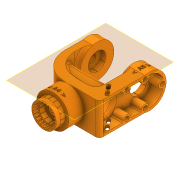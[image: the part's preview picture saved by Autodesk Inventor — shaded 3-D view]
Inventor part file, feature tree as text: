
AUTODESK INVENTOR PART (.ipt)
format: ipt  version: 2020 (Build 240168000, 168)  size: 2,027,008 bytes
history: native  units: in
note: dims shown in document units (in); Inventor stores cm internally (conversion verified against a paired STEP export)
features: sketch x40, extrude x36, projected_geometry x29, chamfer x6, plane x6, fillet x5, emboss x3
ambient origin geometry x8: Origin, YZ Plane, XZ Plane, XY Plane, X Axis, Y Axis, Z Axis, Center Point
bodies: Solid1 (feature_tree)
feature tree (125):
  extrude  "Extrusion1"  Depth=2.0472in
  extrude  "Extrusion2"  Depth=1.1024in
  chamfer  "Chamfer2"  Distance=0.2756in
  extrude  "Extrusion4"  Depth=0.0157in
  extrude  "Extrusion7"  Depth=0.2756in TaperAngle=0.0deg
  chamfer  "Chamfer4"  Distance=0.0394in
  extrude  "Extrusion8"  Depth=0.0157in
  sketch  "Sketch12"  dims[d39=1.4567in d57=0.0394in d58=0.0in]
  plane  "Work Plane1"
  sketch  "Sketch13"  dims[d59=0.315in d60=0.125in d61=0.0137in d67=0.0157in]
  extrude  "Extrusion10"  Depth=0.0394in TaperAngle=0.0deg
  extrude  "Extrusion11"  Depth=0.0866in
  chamfer  "Chamfer5"  Distance=9.4488in Angle=360.0deg
  extrude  "Extrusion12"  Depth=0.2756in TaperAngle=0.0deg
  plane  "Work Plane2"
  extrude  "Extrusion13"  Depth=0.2756in
  plane  "Work Plane3"
  extrude  "Extrusion14"  Depth=1.0236in
  extrude  "Extrusion15"  Depth=0.8858in
  extrude  "Extrusion16"  Depth=0.3937in
  extrude  "Extrusion17"  Depth=1.378in
  sketch  "Sketch21"  dims[d107=0.2756in d108=0.0in d109=0.2756in d110=0.125in d111=0.0137in]
  extrude  "Extrusion19"  Depth=0.5906in
  sketch  "Sketch23"  dims[d112=1.0in d113=0.0in d114=1.0236in]
  extrude  "Extrusion20"  Depth=0.1575in TaperAngle=0.0deg
  extrude  "Extrusion21"  Depth=0.1575in TaperAngle=0.0deg
  extrude  "Extrusion22"  Depth=4.2323in
  extrude  "Extrusion23"  Depth=0.1575in
  extrude  "Extrusion24"  Depth=1.1024in
  extrude  "Extrusion25"  Depth=0.4921in
  extrude  "Extrusion26"  Depth=0.75in
  extrude  "Extrusion27"  Depth=0.2165in TaperAngle=0.0deg
  extrude  "Extrusion28"  Depth=0.1575in
  extrude  "Extrusion29"  Depth=1.1811in
  plane  "Work Plane4"
  extrude  "Extrusion30"  Depth=0.3937in TaperAngle=0.0deg
  fillet  "Fillet1"  Radius=0.3937in
  fillet  "Fillet2"  Radius=0.315in
  extrude  "Extrusion31"  Depth=0.315in TaperAngle=0.0deg
  extrude  "Extrusion32"  Depth=0.315in TaperAngle=0.0deg
  extrude  "Extrusion33"  Depth=0.3937in TaperAngle=0.0deg
  fillet  "Fillet3"  Radius=0.2165in
  extrude  "Extrusion34"  Depth=0.4724in
  chamfer  "Chamfer6"  Distance=0.2756in
  chamfer  "Chamfer7"  Distance=0.0394in
  extrude  "Extrusion35"  Depth=0.001in
  extrude  "Extrusion36"  Depth=1.0in TaperAngle=0.0deg
  fillet  "Fillet5"  Radius=0.1575in
  extrude  "Extrusion38"  Depth=0.315in
  extrude  "Extrusion39"  Depth=0.315in
  extrude  "Extrusion40"  Depth=0.0157in
  fillet  "Fillet7"  Radius=2.3622in
  extrude  "Extrusion41"  Depth=1.0in TaperAngle=0.0deg
  chamfer  "Chamfer8"  Distance=1.0in
  extrude  "Extrusion42"  Depth=0.1969in
  plane  "Work Plane6"
  emboss  "Emboss1"
  emboss  "Emboss2"
  plane  "Work Plane7"
  emboss  "Emboss3"
  sketch  "Sketch1"  dims[d0=0.6299in d1=2.0472in]
  sketch  "Sketch2"  dims[d2=0.9449in d3=0.0in d4=1.1024in]
  sketch  "Sketch4"  dims[d5=1.5748in d6=0.2756in d7=0.0in]
  sketch  "Sketch8"  dims[d11=0.2756in d12=0.125in d13=0.0137in d25=0.0157in]
  projected_geometry  "Projected Loop2"
  sketch  "Sketch10"  dims[d26=6.2992in d28=360.0deg d30=0.2756in d31=0.0in]
  sketch  "Sketch14"  dims[d68=4.7244in d70=360.0deg d72=0.0394in d73=0.0in]
  sketch  "Sketch15"  dims[d83=0.0591in d84=0.0866in]
  projected_geometry  "Projected Loop4"
  sketch  "Sketch16"  dims[d85=0.0827in]
  sketch  "Sketch17"  dims[d86=0.0827in]
  projected_geometry  "Projected Loop5"
  sketch  "Sketch18"  dims[d87=0.0827in d88=9.4488in d90=360.0deg]
  projected_geometry  "Projected Loop6"
  projected_geometry  "Projected Loop7"
  sketch  "Sketch19"  dims[d92=0.2756in]
  projected_geometry  "Projected Loop8"
  projected_geometry  "Projected Loop9"
  sketch  "Sketch20"  dims[d94=9.4488in d95=0.0827in d96=0.0827in d97=0.0827in d98=360.0deg d105=0.2756in d106=0.0in]
  projected_geometry  "Projected Loop10"
  projected_geometry  "Projected Loop11"
  projected_geometry  "Projected Loop12"
  projected_geometry  "Projected Loop13"
  sketch  "Sketch25"  dims[d115=0.7874in d117=0.8858in]
  sketch  "Sketch26"  dims[d118=2.7559in d119=0.3937in]
  projected_geometry  "Projected Loop16"
  projected_geometry  "Projected Loop17"
  sketch  "Sketch27"  dims[d120=0.5906in d121=1.378in]
  projected_geometry  "Projected Loop18"
  projected_geometry  "Projected Loop19"
  sketch  "Sketch28"  dims[d123=3.4941in d124=0.5906in]
  projected_geometry  "Projected Loop20"
  projected_geometry  "Projected Loop21"
  sketch  "Sketch29"  dims[d126=1.9685in d129=0.1575in d130=0.0in]
  projected_geometry  "Projected Loop22"
  projected_geometry  "Projected Loop23"
  sketch  "Sketch30"  dims[d131=-2.0472in d132=0.1575in d133=0.0in]
  projected_geometry  "Projected Loop24"
  sketch  "Sketch31"  dims[d134=2.126in d136=4.2323in]
  sketch  "Sketch32"  dims[d137=0.1575in d138=0.1575in]
  sketch  "Sketch34"  dims[d139=0.4921in d140=0.0in d141=1.1024in]
  projected_geometry  "Projected Loop25"
  sketch  "Sketch35"  dims[d142=1.1614in d143=0.4921in]
  sketch  "Sketch36"  dims[d144=0.3445in d145=0.75in]
  projected_geometry  "Projected Loop26"
  sketch  "Sketch37"  dims[d146=0.1575in d147=0.0in d148=0.2165in d149=0.0in]
  projected_geometry  "Projected Loop27"
  sketch  "Sketch38"  dims[d152=1.0039in d153=0.0in d154=0.1575in]
  projected_geometry  "Projected Loop28"
  sketch  "Sketch39"  dims[d155=0.1575in d160=1.1811in]
  projected_geometry  "Projected Loop29"
  sketch  "Sketch40"  dims[d161=0.1969in d162=0.0in d163=0.315in d164=0.0in d165=0.3937in d166=0.0in d167=0.315in d168=0.0in]
  sketch  "Sketch41"  dims[d169=0.315in d170=0.0in d171=0.315in d172=0.0in]
  projected_geometry  "Projected Loop30"
  sketch  "Sketch43"  dims[d173=0.315in d174=0.0in d175=0.315in d176=0.0in]
  projected_geometry  "Projected Loop31"
  sketch  "Sketch44"  dims[d177=1.1024in d178=0.3937in d179=0.0in d180=0.2165in d181=0.0in]
  sketch  "Sketch45"  dims[d183=-0.0197in d184=0.4724in d185=0.2756in d186=0.0in]
  sketch  "Sketch46"  dims[d187=0.5512in]
  projected_geometry  "Projected Loop32"
  sketch  "Sketch47"  dims[d188=0.2165in d189=0.0394in d190=0.0in]
  projected_geometry  "Projected Loop33"
  sketch  "Sketch48"  dims[d191=0.0394in d192=0.0in d193=0.001in]
  sketch  "Sketch49"  dims[d194=0.001in d195=1.0in d196=0.0in d197=0.1575in]
  sketch  "Sketch50"  dims[d198=1.0in d199=0.0in d200=0.315in d201=0.125in d202=0.0137in d203=0.315in d204=0.125in d205=0.0137in d206=0.0157in d207=2.3622in d209=360.0deg d211=1.0in d212=0.0in d213=1.0in d214=0.0in d221=0.1969in d222=0.1969in d223=0.0in d224=0.1575in d225=0.0787in d226=0.1969in d227=0.0in d229=0.1181in d230=1.0039in d231=0.4134in d232=0.5118in d233=0.0984in d235=0.0197in d236=0.1181in d237=0.1181in d238=0.1969in d239=0.1969in d240=0.0in d241=0.0in d242=0.2362in d243=0.0787in d244=0.0787in d251=0.0787in d252=0.0787in d253=0.2756in d254=0.4724in d255=0.2756in d256=0.4724in d257=0.2756in d258=0.4724in d259=0.2756in d260=0.4724in d261=0.1575in d262=0.0in d263=0.0787in d264=0.125in d265=45.0deg d266=1.0in d267=0.0in d269=0.0394in d270=0.0in d271=0.0394in d272=0.0in d273=0.0394in d274=0.0in]
